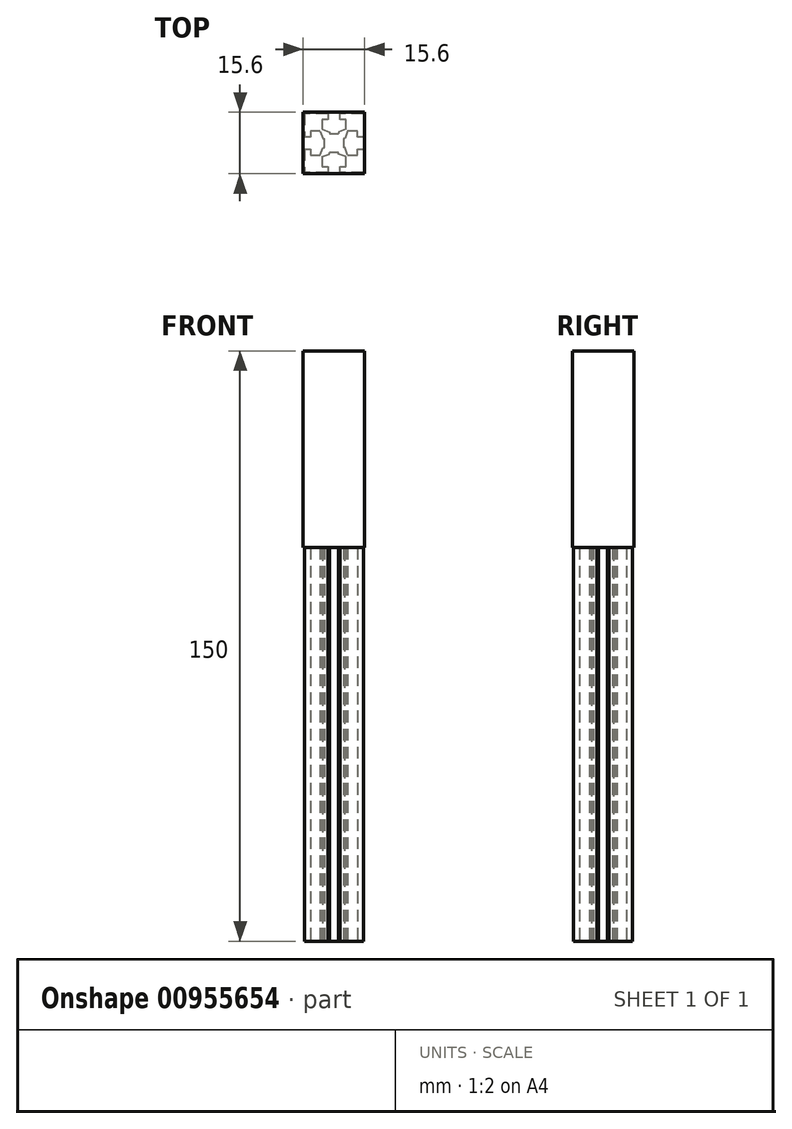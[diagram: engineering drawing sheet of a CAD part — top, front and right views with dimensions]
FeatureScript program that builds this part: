
annotation { "Feature Type Name" : "Feature", "Feature Type Description" : "" }
export const myFeature = defineFeature(function(context is Context, id is Id, definition is map)
    precondition{}
    {
        {
            var Q0;
            Q0=qCreatedBy(makeId("Top.planeOp"),FACE);
            var sketch = newSketch(context, id + "F0", { "sketchPlane" : qUnion([Q0])});
            skLineSegment(sketch, "E0.bottom", {"start": v(7.5, 7.5) * mm, "end": v(1.5, 7.5) * mm});
            skLineSegment(sketch, "E0.left", {"start": v(7.5, 7.5) * mm, "end": v(7.5, 1.5) * mm});
            skLineSegment(sketch, "E0.right", {"start": v(-7.5, 7.5) * mm, "end": v(-7.5, 1.5) * mm});
            skPoint(sketch, "E0.middle", {"position": v(0, 0) * mm});
            skLineSegment(sketch, "E1", {"start": v(7.5, -7.5) * mm, "end": v(1.5, -7.5) * mm});
            skLineSegment(sketch, "E2", {"start": v(1.5, -7.5) * mm, "end": v(1.5, -6) * mm});
            skLineSegment(sketch, "E3", {"start": v(1.5, -6) * mm, "end": v(3, -6) * mm});
            skLineSegment(sketch, "E4", {"start": v(3, -6) * mm, "end": v(3, -3.5) * mm});
            skLineSegment(sketch, "E5", {"start": v(-3, -3.5) * mm, "end": v(-3, -6) * mm});
            skLineSegment(sketch, "E6", {"start": v(-3, -6) * mm, "end": v(-1.5, -6) * mm});
            skLineSegment(sketch, "E7", {"start": v(-1.5, -6) * mm, "end": v(-1.5, -7.5) * mm});
            skLineSegment(sketch, "E8", {"start": v(-1.5, -7.5) * mm, "end": v(-7.5, -7.5) * mm});
            skLineSegment(sketch, "E9.top", {"start": v(1.15, -2.43) * mm, "end": v(-1.15, -2.43) * mm});
            skLineSegment(sketch, "E9.left", {"start": v(1.15, -2.76) * mm, "end": v(1.15, -2.43) * mm});
            skLineSegment(sketch, "E9.right", {"start": v(-1.15, -2.76) * mm, "end": v(-1.15, -2.43) * mm});
            skPoint(sketch, "E9.middle", {"position": v(0, -2.6) * mm});
            skLineSegment(sketch, "E10", {"start": v(-3, -3.5) * mm, "end": v(-1.15, -2.76) * mm});
            skLineSegment(sketch, "E11", {"start": v(3, -3.5) * mm, "end": v(1.15, -2.76) * mm});
            skLineSegment(sketch, "E12.1.0", {"start": v(6, -1.5) * mm, "end": v(7.5, -1.5) * mm});
            skLineSegment(sketch, "E12.1.1", {"start": v(6, -3) * mm, "end": v(6, -1.5) * mm});
            skLineSegment(sketch, "E12.1.2", {"start": v(3.5, -3) * mm, "end": v(6, -3) * mm});
            skLineSegment(sketch, "E12.1.3", {"start": v(3.5, -3) * mm, "end": v(2.76, -1.15) * mm});
            skLineSegment(sketch, "E12.1.4", {"start": v(2.43, 1.15) * mm, "end": v(2.43, -1.15) * mm});
            skLineSegment(sketch, "E12.1.5", {"start": v(2.76, 1.15) * mm, "end": v(2.43, 1.15) * mm});
            skLineSegment(sketch, "E12.1.6", {"start": v(2.76, -1.15) * mm, "end": v(2.43, -1.15) * mm});
            skLineSegment(sketch, "E12.1.7", {"start": v(3.5, 3) * mm, "end": v(2.76, 1.15) * mm});
            skLineSegment(sketch, "E12.1.8", {"start": v(6, 3) * mm, "end": v(3.5, 3) * mm});
            skLineSegment(sketch, "E12.1.9", {"start": v(6, 1.5) * mm, "end": v(6, 3) * mm});
            skLineSegment(sketch, "E12.1.10", {"start": v(7.5, 1.5) * mm, "end": v(6, 1.5) * mm});
            skLineSegment(sketch, "E12.2.0", {"start": v(1.5, 6) * mm, "end": v(1.5, 7.5) * mm});
            skLineSegment(sketch, "E12.2.1", {"start": v(3, 6) * mm, "end": v(1.5, 6) * mm});
            skLineSegment(sketch, "E12.2.2", {"start": v(3, 3.5) * mm, "end": v(3, 6) * mm});
            skLineSegment(sketch, "E12.2.3", {"start": v(3, 3.5) * mm, "end": v(1.15, 2.76) * mm});
            skLineSegment(sketch, "E12.2.4", {"start": v(-1.15, 2.43) * mm, "end": v(1.15, 2.43) * mm});
            skLineSegment(sketch, "E12.2.5", {"start": v(-1.15, 2.76) * mm, "end": v(-1.15, 2.43) * mm});
            skLineSegment(sketch, "E12.2.6", {"start": v(1.15, 2.76) * mm, "end": v(1.15, 2.43) * mm});
            skLineSegment(sketch, "E12.2.7", {"start": v(-3, 3.5) * mm, "end": v(-1.15, 2.76) * mm});
            skLineSegment(sketch, "E12.2.8", {"start": v(-3, 6) * mm, "end": v(-3, 3.5) * mm});
            skLineSegment(sketch, "E12.2.9", {"start": v(-1.5, 6) * mm, "end": v(-3, 6) * mm});
            skLineSegment(sketch, "E12.2.10", {"start": v(-1.5, 7.5) * mm, "end": v(-1.5, 6) * mm});
            skLineSegment(sketch, "E12.3.0", {"start": v(-6, 1.5) * mm, "end": v(-7.5, 1.5) * mm});
            skLineSegment(sketch, "E12.3.1", {"start": v(-6, 3) * mm, "end": v(-6, 1.5) * mm});
            skLineSegment(sketch, "E12.3.2", {"start": v(-3.5, 3) * mm, "end": v(-6, 3) * mm});
            skLineSegment(sketch, "E12.3.3", {"start": v(-3.5, 3) * mm, "end": v(-2.76, 1.15) * mm});
            skLineSegment(sketch, "E12.3.4", {"start": v(-2.43, -1.15) * mm, "end": v(-2.43, 1.15) * mm});
            skLineSegment(sketch, "E12.3.5", {"start": v(-2.76, -1.15) * mm, "end": v(-2.43, -1.15) * mm});
            skLineSegment(sketch, "E12.3.6", {"start": v(-2.76, 1.15) * mm, "end": v(-2.43, 1.15) * mm});
            skLineSegment(sketch, "E12.3.7", {"start": v(-3.5, -3) * mm, "end": v(-2.76, -1.15) * mm});
            skLineSegment(sketch, "E12.3.8", {"start": v(-6, -3) * mm, "end": v(-3.5, -3) * mm});
            skLineSegment(sketch, "E12.3.9", {"start": v(-6, -1.5) * mm, "end": v(-6, -3) * mm});
            skLineSegment(sketch, "E12.3.10", {"start": v(-7.5, -1.5) * mm, "end": v(-6, -1.5) * mm});
            skLineSegment(sketch, "E13.trimOffspring", {"start": v(-1.5, 7.5) * mm, "end": v(-7.5, 7.5) * mm});
            skLineSegment(sketch, "E14.trimOffspring", {"start": v(-7.5, -1.5) * mm, "end": v(-7.5, -7.5) * mm});
            skLineSegment(sketch, "E15.trimOffspring", {"start": v(7.5, -1.5) * mm, "end": v(7.5, -7.5) * mm});
            skSolve(sketch);
        }
        {
            var Q0;
            Q0=makeQuery(id+"F0.imprint","IMPRINT",FACE,{"disambiguationData":[TD([[makeQuery(id+"F0.imprint","IMPRINT",EDGE,{"derivedFrom":sQuery(id+"F0.wireOp",EDGE,"E0.bottom")}),1.0]])]});
            extrude(context, id + "F1", {"entities" : qUnion([Q0]), "endBound" : BoundingType.SYMMETRIC, "depth" : 150 * mm, "offsetDistance" : 25 * mm});
        }
        {
            var Q0;
            Q0=makeQuery(id+"F1.opExtrude","CAP_FACE",FACE,{"disambiguationData":[OSD([sQuery(id+"F0.wireOp",EDGE,"E0.bottom"),sQuery(id+"F0.wireOp",EDGE,"E0.left"),sQuery(id+"F0.wireOp",EDGE,"E0.right"),sQuery(id+"F0.wireOp",EDGE,"E1"),sQuery(id+"F0.wireOp",EDGE,"E2"),sQuery(id+"F0.wireOp",EDGE,"E3"),sQuery(id+"F0.wireOp",EDGE,"E4"),sQuery(id+"F0.wireOp",EDGE,"E5"),sQuery(id+"F0.wireOp",EDGE,"E6"),sQuery(id+"F0.wireOp",EDGE,"E7"),sQuery(id+"F0.wireOp",EDGE,"E8"),sQuery(id+"F0.wireOp",EDGE,"E9.top"),sQuery(id+"F0.wireOp",EDGE,"E9.left"),sQuery(id+"F0.wireOp",EDGE,"E9.right"),sQuery(id+"F0.wireOp",EDGE,"E10"),sQuery(id+"F0.wireOp",EDGE,"E11"),sQuery(id+"F0.wireOp",EDGE,"E12.1.0"),sQuery(id+"F0.wireOp",EDGE,"E12.1.1"),sQuery(id+"F0.wireOp",EDGE,"E12.1.2"),sQuery(id+"F0.wireOp",EDGE,"E12.1.3"),sQuery(id+"F0.wireOp",EDGE,"E12.1.4"),sQuery(id+"F0.wireOp",EDGE,"E12.1.5"),sQuery(id+"F0.wireOp",EDGE,"E12.1.6"),sQuery(id+"F0.wireOp",EDGE,"E12.1.7"),sQuery(id+"F0.wireOp",EDGE,"E12.1.8"),sQuery(id+"F0.wireOp",EDGE,"E12.1.9"),sQuery(id+"F0.wireOp",EDGE,"E12.1.10"),sQuery(id+"F0.wireOp",EDGE,"E12.2.0"),sQuery(id+"F0.wireOp",EDGE,"E12.2.1"),sQuery(id+"F0.wireOp",EDGE,"E12.2.2"),sQuery(id+"F0.wireOp",EDGE,"E12.2.3"),sQuery(id+"F0.wireOp",EDGE,"E12.2.4"),sQuery(id+"F0.wireOp",EDGE,"E12.2.5"),sQuery(id+"F0.wireOp",EDGE,"E12.2.6"),sQuery(id+"F0.wireOp",EDGE,"E12.2.7"),sQuery(id+"F0.wireOp",EDGE,"E12.2.8"),sQuery(id+"F0.wireOp",EDGE,"E12.2.9"),sQuery(id+"F0.wireOp",EDGE,"E12.2.10"),sQuery(id+"F0.wireOp",EDGE,"E12.3.0"),sQuery(id+"F0.wireOp",EDGE,"E12.3.1"),sQuery(id+"F0.wireOp",EDGE,"E12.3.2"),sQuery(id+"F0.wireOp",EDGE,"E12.3.3"),sQuery(id+"F0.wireOp",EDGE,"E12.3.4"),sQuery(id+"F0.wireOp",EDGE,"E12.3.5"),sQuery(id+"F0.wireOp",EDGE,"E12.3.6"),sQuery(id+"F0.wireOp",EDGE,"E12.3.7"),sQuery(id+"F0.wireOp",EDGE,"E12.3.8"),sQuery(id+"F0.wireOp",EDGE,"E12.3.9"),sQuery(id+"F0.wireOp",EDGE,"E12.3.10"),sQuery(id+"F0.wireOp",EDGE,"E13.trimOffspring"),sQuery(id+"F0.wireOp",EDGE,"E14.trimOffspring"),sQuery(id+"F0.wireOp",EDGE,"E15.trimOffspring")])],"isStart":false});
            var sketch = newSketch(context, id + "F2", { "sketchPlane" : qUnion([Q0])});
            skLineSegment(sketch, "E16.bottom", {"start": v(7.8, 7.8) * mm, "end": v(-7.8, 7.8) * mm});
            skLineSegment(sketch, "E16.top", {"start": v(7.8, -7.8) * mm, "end": v(-7.8, -7.8) * mm});
            skLineSegment(sketch, "E16.left", {"start": v(7.8, 7.8) * mm, "end": v(7.8, -7.8) * mm});
            skLineSegment(sketch, "E16.right", {"start": v(-7.8, 7.8) * mm, "end": v(-7.8, -7.8) * mm});
            skPoint(sketch, "E16.middle", {"position": v(0, 0) * mm});
            skSolve(sketch);
        }
        {
            var Q0;
            Q0=makeQuery(id+"F2.imprint","IMPRINT",FACE,{"disambiguationData":[TD([[makeQuery(id+"F2.imprint","IMPRINT",EDGE,{"derivedFrom":sQuery(id+"F2.wireOp",EDGE,"E16.bottom")}),1.0]])]});
            extrude(context, id + "F3", {"entities" : qUnion([Q0]), "operationType" : NewBodyOperationType.ADD, "oppositeDirection" : true, "depth" : 50 * mm, "offsetDistance" : 25 * mm});
        }
    });
